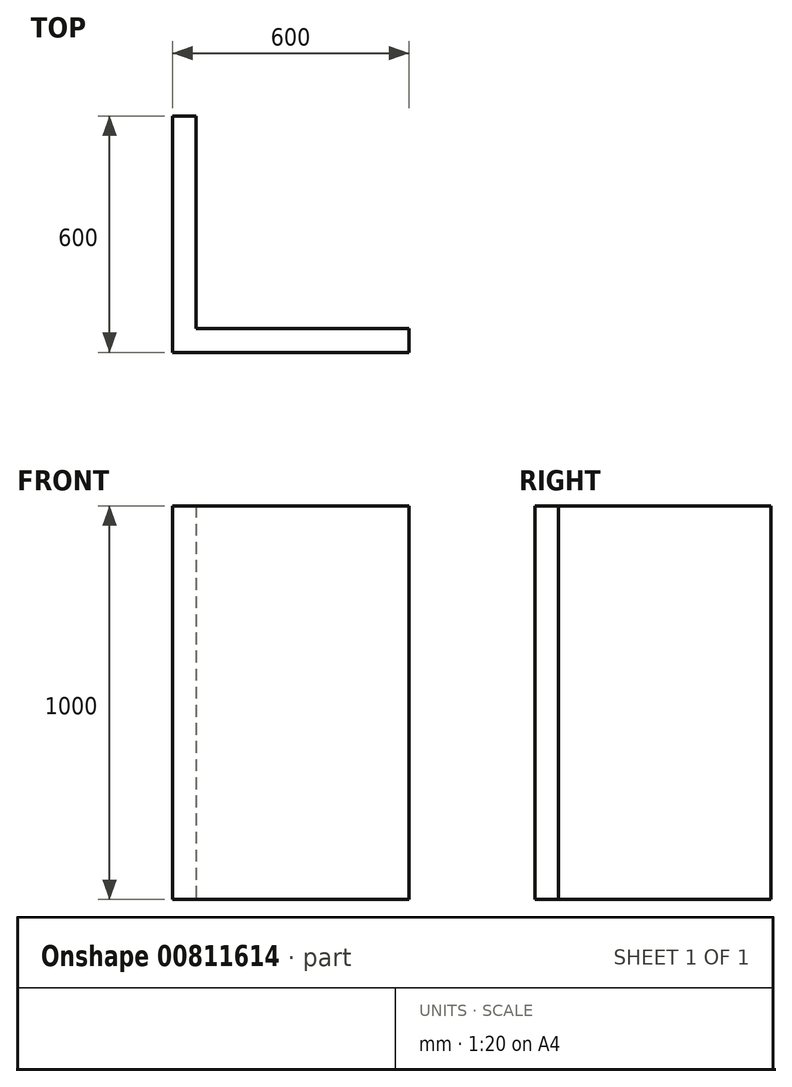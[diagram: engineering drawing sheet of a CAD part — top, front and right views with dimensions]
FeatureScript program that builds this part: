
annotation { "Feature Type Name" : "Feature", "Feature Type Description" : "" }
export const myFeature = defineFeature(function(context is Context, id is Id, definition is map)
    precondition{}
    {
        {
            var Q0;
            Q0=qCreatedBy(makeId("Top.planeOp"),FACE);
            var sketch = newSketch(context, id + "F0", { "sketchPlane" : qUnion([Q0])});
            skLineSegment(sketch, "E0.top", {"start": v(-4392.96, -2296.23) * mm, "end": v(-3792.96, -2296.23) * mm});
            skLineSegment(sketch, "E0.left", {"start": v(-4392.96, -1696.23) * mm, "end": v(-4392.96, -2296.23) * mm});
            skLineSegment(sketch, "E1", {"start": v(-3792.96, -2296.23) * mm, "end": v(-3792.96, -2236.23) * mm});
            skLineSegment(sketch, "E2", {"start": v(-3792.96, -2236.23) * mm, "end": v(-4332.96, -2236.23) * mm});
            skLineSegment(sketch, "E3", {"start": v(-4332.96, -2236.23) * mm, "end": v(-4332.96, -1696.23) * mm});
            skLineSegment(sketch, "E4", {"start": v(-4332.96, -1696.23) * mm, "end": v(-4392.96, -1696.23) * mm});
            skSolve(sketch);
        }
        {
            var Q0;
            Q0 = qSketchRegion(id + "F0", true);
            extrude(context, id + "F1", {"entities" : qUnion([Q0]), "depth" : 1000 * mm, "offsetDistance" : 25 * mm});
        }
    });
